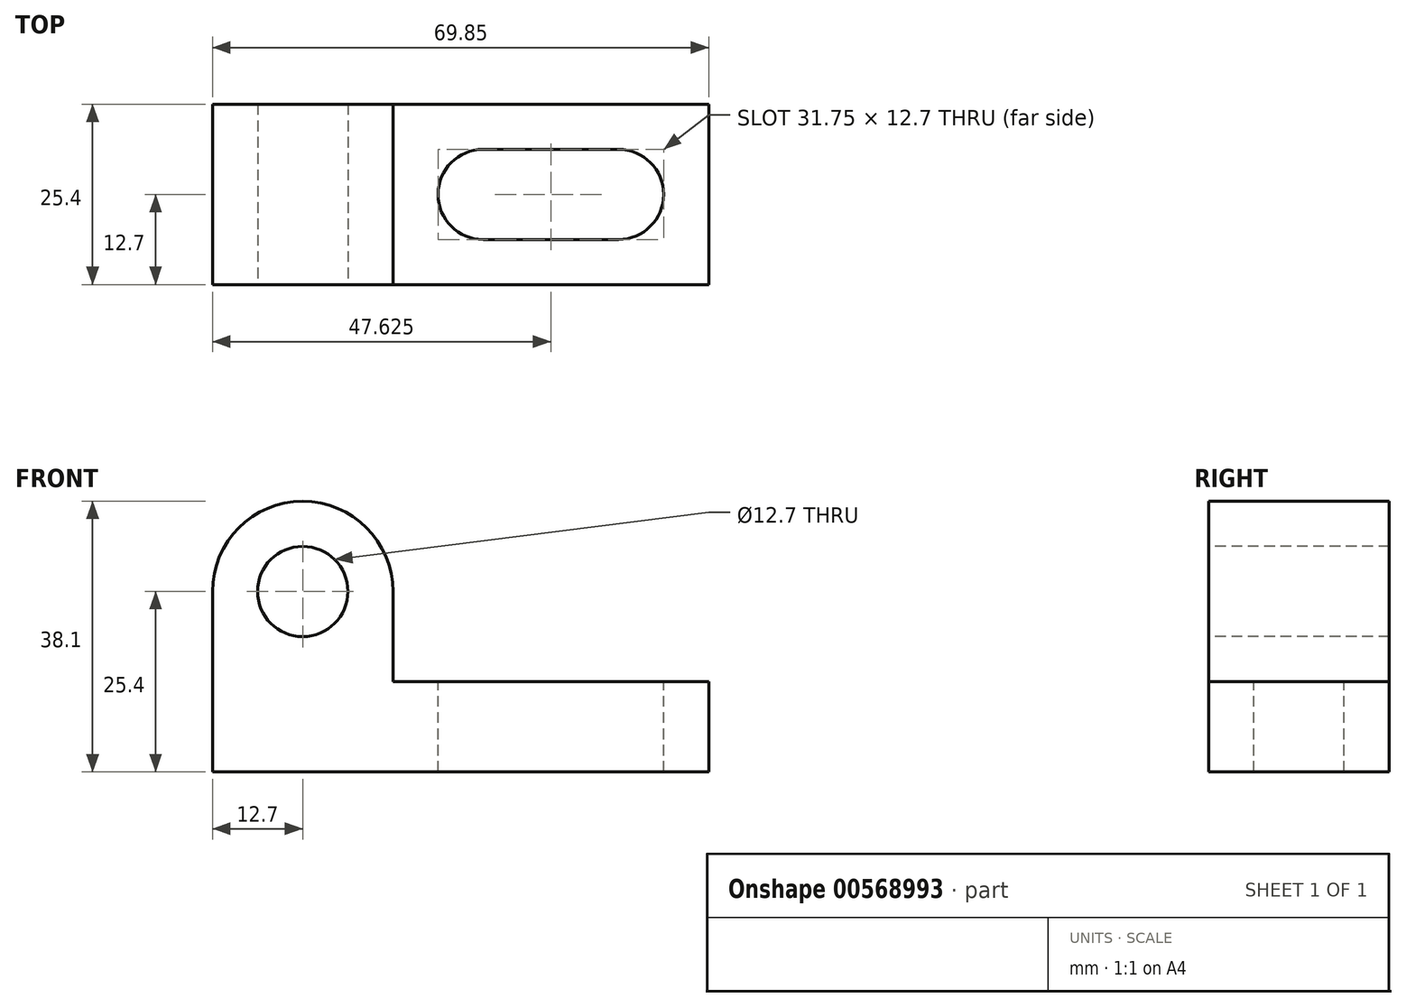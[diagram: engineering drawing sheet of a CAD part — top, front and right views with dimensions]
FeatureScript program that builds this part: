
annotation { "Feature Type Name" : "Feature", "Feature Type Description" : "" }
export const myFeature = defineFeature(function(context is Context, id is Id, definition is map)
    precondition{}
    {
        {
            var Q0;
            Q0=qCreatedBy(makeId("Front.planeOp"),FACE);
            var sketch = newSketch(context, id + "F0", { "sketchPlane" : qUnion([Q0])});
            skLineSegment(sketch, "E0", {"start": v(0, 38.1) * mm, "end": v(0, 0) * mm});
            skLineSegment(sketch, "E1", {"start": v(0, 0) * mm, "end": v(69.85, 0) * mm});
            skLineSegment(sketch, "E2", {"start": v(0, 38.1) * mm, "end": v(69.85, 38.1) * mm});
            skLineSegment(sketch, "E3", {"start": v(69.85, 38.1) * mm, "end": v(69.85, 0) * mm});
            skSolve(sketch);
        }
        {
            var Q0;
            Q0=makeQuery(id+"F0.imprint","IMPRINT",FACE,{"disambiguationData":[TD([[makeQuery(id+"F0.imprint","IMPRINT",EDGE,{"derivedFrom":sQuery(id+"F0.wireOp",EDGE,"E0")}),1.0]])]});
            extrude(context, id + "F1", {"entities" : qUnion([Q0]), "depth" : 25.4 * mm, "offsetDistance" : 25.4 * mm});
        }
        {
            var Q0;
            Q0=makeQuery(id+"F1.opExtrude","CAP_FACE",FACE,{"disambiguationData":[OSD([sQuery(id+"F0.wireOp",EDGE,"E0"),sQuery(id+"F0.wireOp",EDGE,"E1"),sQuery(id+"F0.wireOp",EDGE,"E2"),sQuery(id+"F0.wireOp",EDGE,"E3")])],"isStart":false});
            var sketch = newSketch(context, id + "F2", { "sketchPlane" : qUnion([Q0])});
            skLineSegment(sketch, "E4", {"start": v(25.4, 25.4) * mm, "end": v(25.4, 12.7) * mm});
            skLineSegment(sketch, "E5", {"start": v(25.4, 12.7) * mm, "end": v(69.85, 12.7) * mm});
            skLineSegment(sketch, "E6", {"start": v(69.85, 12.7) * mm, "end": v(69.85, 0) * mm});
            skArc(sketch, "E7", {"start": v(25.4, 25.4) * mm, "mid": v(12.7, 38.1) * mm, "end": v(0, 25.4) * mm});
            skLineSegment(sketch, "E8", {"start": v(0, 0) * mm, "end": v(0, 25.4) * mm});
            skCircle(sketch, "E9", {"center": v(12.7, 25.4) * mm, "radius": 6.35 * mm});
            skSolve(sketch);
        }
        {
            var Q0;
            Q0=makeQuery(id+"F2.imprint","IMPRINT",FACE,{"disambiguationData":[TD([[makeQuery(id+"F2.imprint","IMPRINT",EDGE,{"derivedFrom":sQuery(id+"F2.wireOp",EDGE,"E9")}),1.0]])]});
            var Q1;
            {var subQ5=sQuery(id+"F2.wireOp",EDGE,"E4");Q1=makeQuery(id+"F2.imprint","IMPRINT",FACE,{"disambiguationData":[TD([[makeQuery(id+"F2.imprint","IMPRINT",EDGE,{"derivedFrom":subQ5}),1.0]])]});}
            var Q2;
            {var subQ1=makeQuery(id+"F1.opExtrude","CAP_EDGE",EDGE,{"disambiguationData":[OSD([sQuery(id+"F0.wireOp",EDGE,"E0")])],"isStart":false});var subQ3=makeQuery(id+"F1.opExtrude","CAP_EDGE",EDGE,{"disambiguationData":[OSD([sQuery(id+"F0.wireOp",EDGE,"E2")])],"isStart":false});var subQ5=makeQuery(id+"F2.imprint","INTERSECT",VERTEX,{"derivedFrom":[subQ1,subQ3]});Q2=makeQuery(id+"F2.imprint","IMPRINT",FACE,{"disambiguationData":[TD([[makeQuery(id+"F2.imprint","IMPRINT",EDGE,{"disambiguationData":[TD([[subQ5,-1.0]])],"derivedFrom":subQ3}),-1.0]])]});}
            extrude(context, id + "F3", {"entities" : qUnion([Q0, Q1, Q2]), "operationType" : NewBodyOperationType.REMOVE, "oppositeDirection" : true, "depth" : 25.4 * mm, "offsetDistance" : 25.4 * mm});
        }
        {
            var Q0;
            Q0=makeQuery(id+"F3.boolean.opBoolean","COPY",FACE,{"derivedFrom":makeQuery(id+"F3.opExtrude","SWEPT_FACE",FACE,{"disambiguationData":[OSD([sQuery(id+"F2.wireOp",EDGE,"E5")])]})});
            var sketch = newSketch(context, id + "F4", { "sketchPlane" : qUnion([Q0])});
            skLineSegment(sketch, "E10", {"start": v(25.4, 0) * mm, "end": v(57.15, 0) * mm});
            skLineSegment(sketch, "E11", {"start": v(25.4, -25.4) * mm, "end": v(57.15, -25.4) * mm});
            skArc(sketch, "E12", {"start": v(57.15, 0) * mm, "mid": v(69.85, -12.7) * mm, "end": v(57.15, -25.4) * mm});
            skCircle(sketch, "E13", {"center": v(57.15, -12.7) * mm, "radius": 6.35 * mm});
            skCircle(sketch, "E14", {"center": v(38.1, -12.7) * mm, "radius": 6.35 * mm});
            skLineSegment(sketch, "E15", {"start": v(57.15, -6.35) * mm, "end": v(38.1, -6.35) * mm});
            skLineSegment(sketch, "E16", {"start": v(38.1, -19.05) * mm, "end": v(57.15, -19.05) * mm});
            skSolve(sketch);
        }
        {
            var Q0;
            {var subQ0=sQuery(id+"F4.wireOp",EDGE,"E15");Q0=makeQuery(id+"F4.imprint","IMPRINT",FACE,{"disambiguationData":[TD([[makeQuery(id+"F4.imprint","IMPRINT",EDGE,{"derivedFrom":subQ0}),1.0]])]});}
            var Q1;
            {var subQ0=sQuery(id+"F4.wireOp",EDGE,"E14");var subQ1=makeQuery(id+"F4.imprint","INTERSECT",VERTEX,{"derivedFrom":[subQ0,sQuery(id+"F4.wireOp",EDGE,"E15")]});Q1=makeQuery(id+"F4.imprint","IMPRINT",FACE,{"disambiguationData":[TD([[makeQuery(id+"F4.imprint","IMPRINT",EDGE,{"disambiguationData":[TD([[subQ1,-1.0]])],"derivedFrom":subQ0}),1.0]])]});}
            var Q2;
            {var subQ0=sQuery(id+"F4.wireOp",EDGE,"E13");var subQ1=makeQuery(id+"F4.imprint","INTERSECT",VERTEX,{"derivedFrom":[subQ0,sQuery(id+"F4.wireOp",EDGE,"E15")]});Q2=makeQuery(id+"F4.imprint","IMPRINT",FACE,{"disambiguationData":[TD([[makeQuery(id+"F4.imprint","IMPRINT",EDGE,{"disambiguationData":[TD([[subQ1,-1.0]])],"derivedFrom":subQ0}),1.0]])]});}
            extrude(context, id + "F5", {"entities" : qUnion([Q0, Q1, Q2]), "operationType" : NewBodyOperationType.REMOVE, "oppositeDirection" : true, "depth" : 12.7 * mm, "offsetDistance" : 25.4 * mm});
        }
    });
